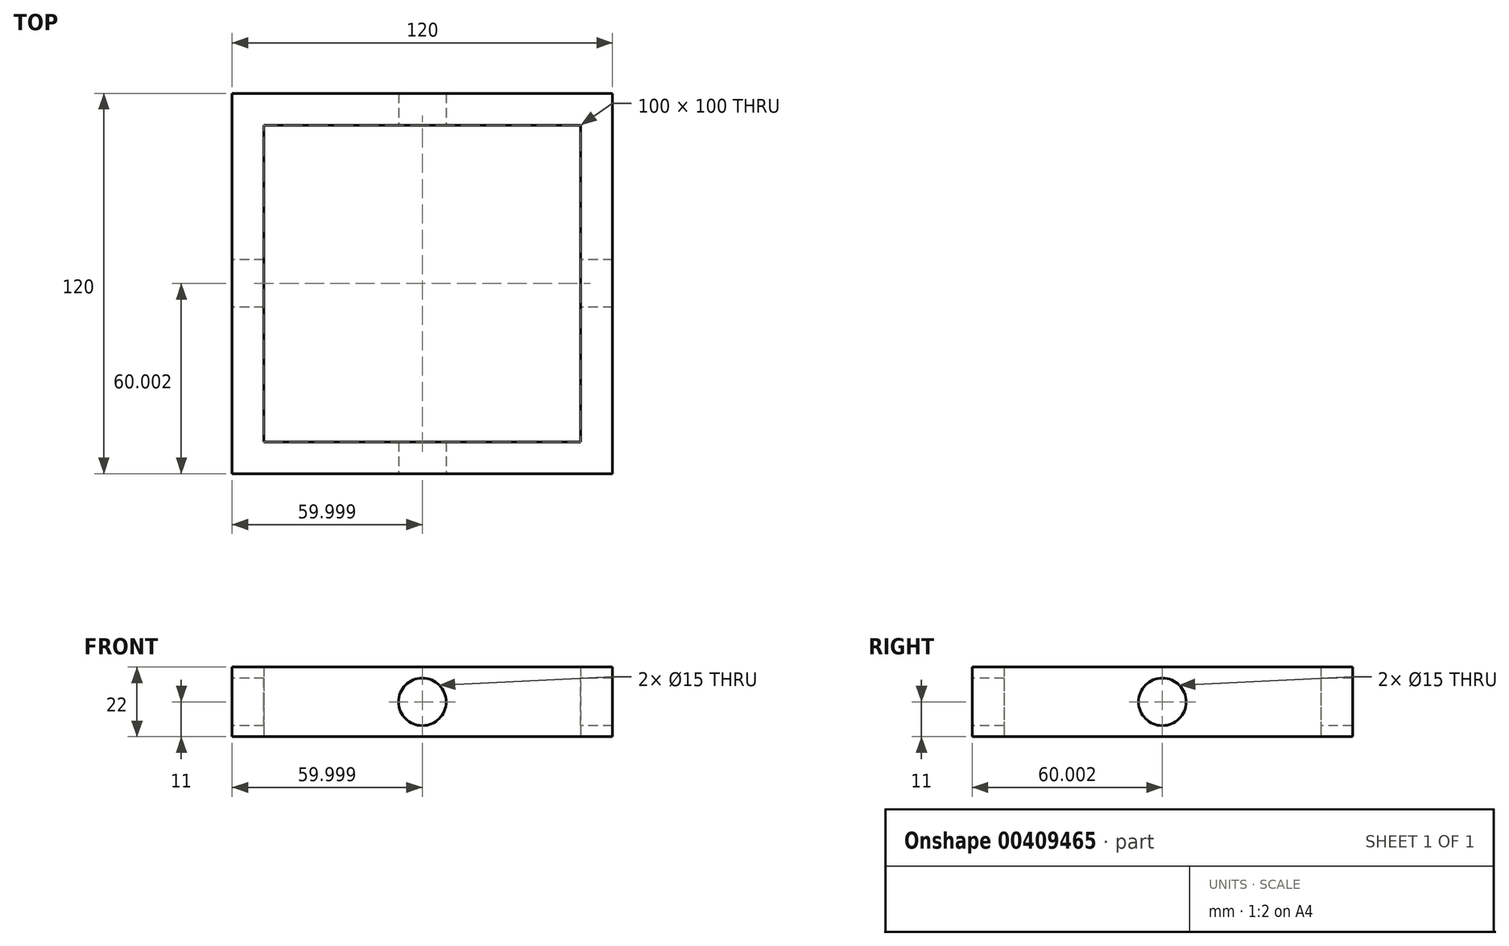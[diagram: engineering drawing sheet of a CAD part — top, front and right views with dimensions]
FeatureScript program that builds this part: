
annotation { "Feature Type Name" : "Feature", "Feature Type Description" : "" }
export const myFeature = defineFeature(function(context is Context, id is Id, definition is map)
    precondition{}
    {
        {
            var Q0;
            Q0=qCreatedBy(makeId("Top.planeOp"),FACE);
            var sketch = newSketch(context, id + "F0", { "sketchPlane" : qUnion([Q0])});
            skLineSegment(sketch, "E0.bottom", {"start": v(6.5, 99.73) * mm, "end": v(106.5, 99.73) * mm});
            skLineSegment(sketch, "E0.top", {"start": v(6.5, -0.27) * mm, "end": v(106.5, -0.27) * mm});
            skLineSegment(sketch, "E0.left", {"start": v(6.5, 99.73) * mm, "end": v(6.5, -0.27) * mm});
            skLineSegment(sketch, "E0.right", {"start": v(106.5, 99.73) * mm, "end": v(106.5, -0.27) * mm});
            skLineSegment(sketch, "E1.bottom", {"start": v(-3.5, 109.73) * mm, "end": v(116.5, 109.73) * mm});
            skLineSegment(sketch, "E1.top", {"start": v(-3.5, -10.27) * mm, "end": v(116.5, -10.27) * mm});
            skLineSegment(sketch, "E1.left", {"start": v(-3.5, 109.73) * mm, "end": v(-3.5, -10.27) * mm});
            skLineSegment(sketch, "E1.right", {"start": v(116.5, 109.73) * mm, "end": v(116.5, -10.27) * mm});
            skSolve(sketch);
        }
        {
            var Q0;
            Q0=makeQuery(id+"F0.imprint","IMPRINT",FACE,{"disambiguationData":[TD([[makeQuery(id+"F0.imprint","IMPRINT",EDGE,{"derivedFrom":sQuery(id+"F0.wireOp",EDGE,"E0.bottom")}),1.0]])]});
            extrude(context, id + "F1", {"entities" : qUnion([Q0]), "depth" : 22 * mm});
        }
        {
            var Q0;
            Q0=makeQuery(id+"F1.opExtrude","SWEPT_FACE",FACE,{"disambiguationData":[OSD([sQuery(id+"F0.wireOp",EDGE,"E1.top")])]});
            var sketch = newSketch(context, id + "F2", { "sketchPlane" : qUnion([Q0])});
            skCircle(sketch, "E2", {"center": v(56.5, 11) * mm, "radius": 7.5 * mm});
            skPoint(sketch, "E2.centerSnap0", {"position": v(56.5, 0) * mm});
            skPoint(sketch, "E2.centerSnap1", {"position": v(116.5, 11) * mm});
            skSolve(sketch);
        }
        {
            var Q0;
            Q0=makeQuery(id+"F2.imprint","IMPRINT",FACE,{"disambiguationData":[TD([[makeQuery(id+"F2.imprint","IMPRINT",EDGE,{"derivedFrom":sQuery(id+"F2.wireOp",EDGE,"E2")}),1.0]])]});
            extrude(context, id + "F3", {"entities" : qUnion([Q0]), "operationType" : NewBodyOperationType.REMOVE, "oppositeDirection" : true, "depth" : 237 * mm});
        }
        {
            var Q0;
            Q0=makeQuery(id+"F1.opExtrude","SWEPT_FACE",FACE,{"disambiguationData":[OSD([sQuery(id+"F0.wireOp",EDGE,"E1.left")])]});
            var sketch = newSketch(context, id + "F4", { "sketchPlane" : qUnion([Q0])});
            skCircle(sketch, "E3", {"center": v(-49.73, 11) * mm, "radius": 7.5 * mm});
            skPoint(sketch, "E3.centerSnap0", {"position": v(10.27, 11) * mm});
            skPoint(sketch, "E3.centerSnap1", {"position": v(-49.73, 22) * mm});
            skSolve(sketch);
        }
        {
            var Q0;
            Q0=makeQuery(id+"F4.imprint","IMPRINT",FACE,{"disambiguationData":[TD([[makeQuery(id+"F4.imprint","IMPRINT",EDGE,{"derivedFrom":sQuery(id+"F4.wireOp",EDGE,"E3")}),1.0]])]});
            var Q1;
            Q1=sQuery(id+"F4.wireOp",EDGE,"E3");
            extrude(context, id + "F5", {"entities" : qUnion([Q0]), "operationType" : NewBodyOperationType.REMOVE, "surfaceEntities" : qUnion([Q1]), "oppositeDirection" : true, "depth" : 185 * mm});
        }
    });
